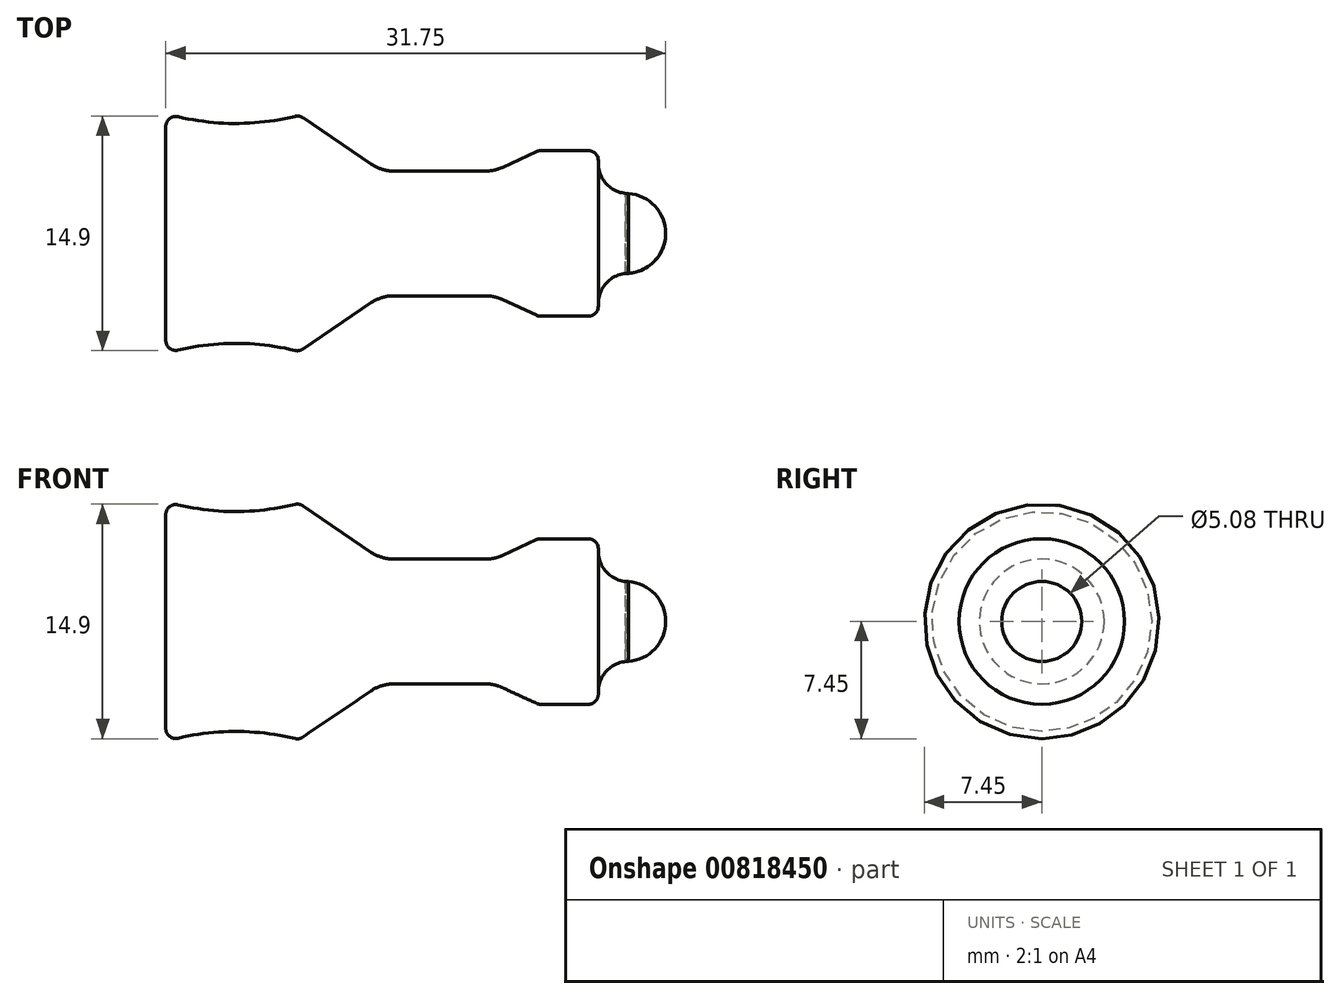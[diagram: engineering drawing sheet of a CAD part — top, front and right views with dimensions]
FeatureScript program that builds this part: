
annotation { "Feature Type Name" : "Feature", "Feature Type Description" : "" }
export const myFeature = defineFeature(function(context is Context, id is Id, definition is map)
    precondition{}
    {
        {
            var Q0;
            Q0=qCreatedBy(makeId("Top.planeOp"),FACE);
            var sketch = newSketch(context, id + "F0", { "sketchPlane" : qUnion([Q0])});
            skLineSegment(sketch, "E0", {"start": v(0, 0) * mm, "end": v(-31.75, 0) * mm});
            skLineSegment(sketch, "E1", {"start": v(-31.75, 0) * mm, "end": v(-31.75, 6.8) * mm});
            skPoint(sketch, "E2.endSnap0", {"position": v(-27.51, 7.56) * mm});
            skArc(sketch, "E3", {"start": v(-30.97, 7.41) * mm, "mid": v(-27.26, 6.99) * mm, "end": v(-23.55, 7.44) * mm});
            skPoint(sketch, "E2.end.orphan", {"position": v(-27.51, 6.99) * mm});
            skPoint(sketch, "E2.start.orphan", {"position": v(-27.51, 7.56) * mm});
            skArc(sketch, "E4", {"start": v(0, 0) * mm, "mid": v(-0.74, 1.8) * mm, "end": v(-2.54, 2.54) * mm});
            skLineSegment(sketch, "E5", {"start": v(-4.28, 4.45) * mm, "end": v(-4.28, 4.62) * mm});
            skLineSegment(sketch, "E6", {"start": v(-4.91, 5.26) * mm, "end": v(-7.95, 5.26) * mm});
            skLineSegment(sketch, "E7", {"start": v(-8.22, 5.2) * mm, "end": v(-10.37, 4.2) * mm});
            skLineSegment(sketch, "E8", {"start": v(-11.44, 3.96) * mm, "end": v(-17.28, 3.96) * mm});
            skLineSegment(sketch, "E9", {"start": v(-18.7, 4.4) * mm, "end": v(-23.04, 7.34) * mm});
            skLineSegment(sketch, "E10", {"start": v(-2.37, 2.54) * mm, "end": v(-2.54, 2.54) * mm});
            skPoint(sketch, "E11.visualSharp", {"position": v(-4.28, 2.54) * mm});
            skArc(sketch, "E11.filletArc", {"start": v(-4.28, 4.45) * mm, "mid": v(-3.72, 3.1) * mm, "end": v(-2.37, 2.54) * mm});
            skPoint(sketch, "E12.visualSharp", {"position": v(-4.28, 5.26) * mm});
            skArc(sketch, "E12.filletArc", {"start": v(-4.28, 4.62) * mm, "mid": v(-4.46, 5.07) * mm, "end": v(-4.91, 5.26) * mm});
            skPoint(sketch, "E13.visualSharp", {"position": v(-8.09, 5.26) * mm});
            skArc(sketch, "E13.filletArc", {"start": v(-7.95, 5.26) * mm, "mid": v(-8.09, 5.24) * mm, "end": v(-8.22, 5.2) * mm});
            skPoint(sketch, "E14.visualSharp", {"position": v(-31.75, 7.62) * mm});
            skArc(sketch, "E14.filletArc", {"start": v(-30.97, 7.41) * mm, "mid": v(-31.5, 7.3) * mm, "end": v(-31.75, 6.8) * mm});
            skPoint(sketch, "E15.visualSharp", {"position": v(-23.28, 7.5) * mm});
            skArc(sketch, "E15.filletArc", {"start": v(-23.04, 7.34) * mm, "mid": v(-23.28, 7.44) * mm, "end": v(-23.55, 7.44) * mm});
            skPoint(sketch, "E16.visualSharp", {"position": v(-18.06, 3.96) * mm});
            skArc(sketch, "E16.filletArc", {"start": v(-18.7, 4.4) * mm, "mid": v(-18.02, 4.07) * mm, "end": v(-17.28, 3.96) * mm});
            skPoint(sketch, "E17.visualSharp", {"position": v(-10.88, 3.96) * mm});
            skArc(sketch, "E17.filletArc", {"start": v(-11.44, 3.96) * mm, "mid": v(-10.9, 4.02) * mm, "end": v(-10.37, 4.2) * mm});
            skSolve(sketch);
        }
        {
            var Q0;
            Q0=makeQuery(id+"F0.imprint","IMPRINT",FACE,{"disambiguationData":[TD([[makeQuery(id+"F0.imprint","IMPRINT",EDGE,{"derivedFrom":sQuery(id+"F0.wireOp",EDGE,"E0")}),-1.0]])]});
            var Q1;
            Q1=sQuery(id+"F0.wireOp",EDGE,"E0");
            revolve(context, id + "F1", {"surfaceOperationType" : NewSurfaceOperationType.NEW, "entities" : qUnion([Q0]), "axis" : qUnion([Q1]), "revolveType" : RevolveType.FULL});
        }
    });
